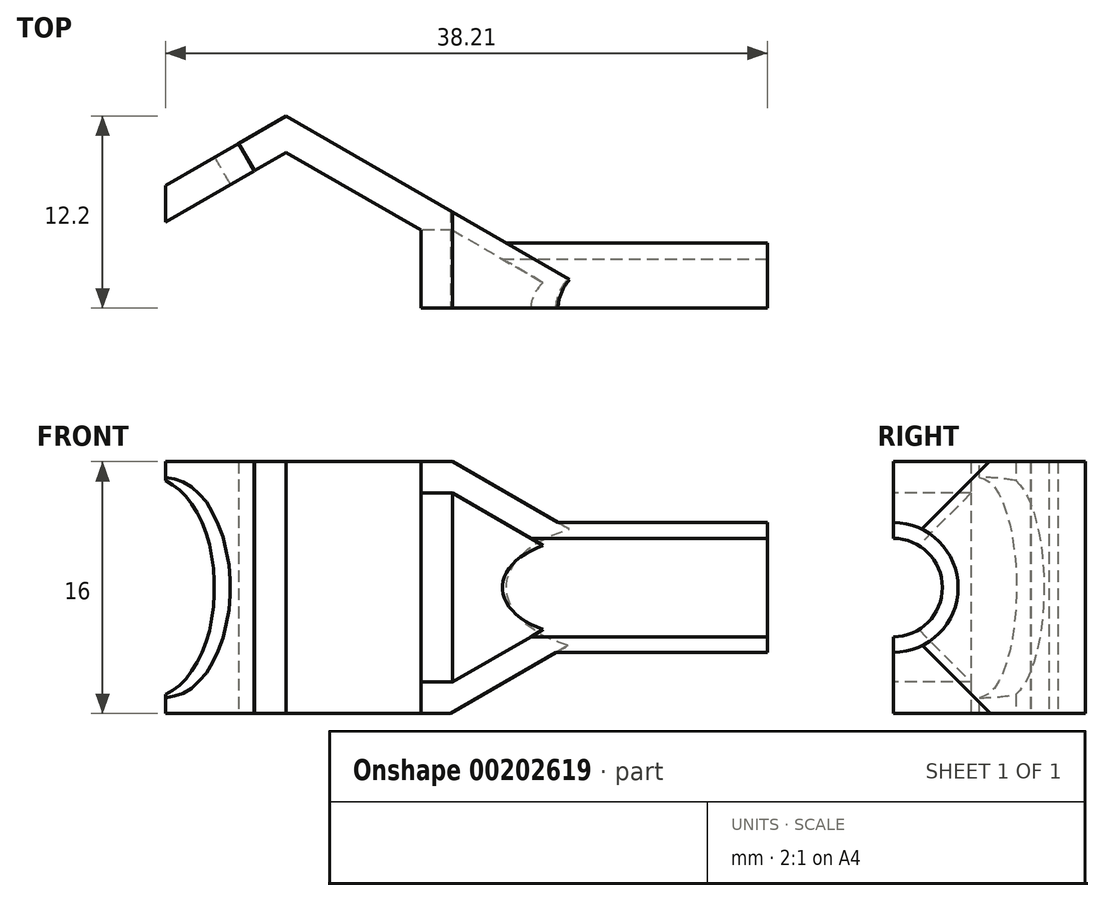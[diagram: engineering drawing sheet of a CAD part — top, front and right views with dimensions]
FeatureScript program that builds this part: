
annotation { "Feature Type Name" : "Feature", "Feature Type Description" : "" }
export const myFeature = defineFeature(function(context is Context, id is Id, definition is map)
    precondition{}
    {
        {
            var Q0;
            Q0=qCreatedBy(makeId("Top.planeOp"),FACE);
            var sketch = newSketch(context, id + "F0", { "sketchPlane" : qUnion([Q0])});
            skCircle(sketch, "E0.cCircle", {"center": v(0, 0) * mm, "radius": 9.89 * mm, "construction": true});
            skLineSegment(sketch, "E0.4", {"start": v(-2, 8.73) * mm, "end": v(0, 9.89) * mm});
            skLineSegment(sketch, "E0.5", {"start": v(0, 9.89) * mm, "end": v(8.56, 4.94) * mm});
            skLineSegment(sketch, "E1", {"start": v(0, 0) * mm, "end": v(-2, 0) * mm, "construction": true});
            skLineSegment(sketch, "E2", {"start": v(-2, 0) * mm, "end": v(-2, 14.12) * mm, "construction": true});
            skLineSegment(sketch, "E3.1", {"start": v(0, 12.2) * mm, "end": v(10.44, 6.17) * mm});
            skLineSegment(sketch, "E3.2", {"start": v(-3.02, 10.45) * mm, "end": v(0, 12.2) * mm});
            skLineSegment(sketch, "E4", {"start": v(-3.02, 10.45) * mm, "end": v(-2, 8.73) * mm});
            skPoint(sketch, "E5.orphan", {"position": v(14.51, 0) * mm});
            skPoint(sketch, "E3.0.end.orphan", {"position": v(10.5, 0) * mm});
            skLineSegment(sketch, "E6", {"start": v(8.56, 0) * mm, "end": v(10.5, 0) * mm});
            skLineSegment(sketch, "E7", {"start": v(8.56, 4.94) * mm, "end": v(8.56, 0) * mm});
            skLineSegment(sketch, "E8", {"start": v(10.44, 6.17) * mm, "end": v(21.13, 0) * mm});
            skLineSegment(sketch, "E9", {"start": v(10.5, 0) * mm, "end": v(21.13, 0) * mm});
            skSolve(sketch);
        }
        {
            var Q0;
            Q0=makeQuery(id+"F0.imprint","IMPRINT",FACE,{"disambiguationData":[TD([[makeQuery(id+"F0.imprint","IMPRINT",EDGE,{"derivedFrom":sQuery(id+"F0.wireOp",EDGE,"E0.4")}),1.0]])]});
            extrude(context, id + "F1", {"entities" : qUnion([Q0]), "depth" : 16 * mm});
        }
        {
            var Q0;
            Q0=makeQuery(id+"F1.opExtrude","SWEPT_FACE",FACE,{"disambiguationData":[OSD([sQuery(id+"F0.wireOp",EDGE,"E6"),sQuery(id+"F0.wireOp",EDGE,"E9")])]});
            var sketch = newSketch(context, id + "F2", { "sketchPlane" : qUnion([Q0])});
            skLineSegment(sketch, "E10", {"start": v(8.56, 16) * mm, "end": v(10.56, 16) * mm, "construction": true});
            skLineSegment(sketch, "E11", {"start": v(10.56, 16) * mm, "end": v(21.54, 9.66) * mm});
            skLineSegment(sketch, "E12", {"start": v(10.44, 0) * mm, "end": v(21.43, 6.35) * mm});
            skLineSegment(sketch, "E13", {"start": v(10.56, 16) * mm, "end": v(22.24, 16) * mm});
            skLineSegment(sketch, "E14", {"start": v(22.24, 16) * mm, "end": v(21.54, 9.66) * mm});
            skLineSegment(sketch, "E15", {"start": v(10.44, 0) * mm, "end": v(21.97, 0) * mm});
            skLineSegment(sketch, "E16", {"start": v(21.97, 0) * mm, "end": v(21.43, 6.35) * mm});
            skSolve(sketch);
        }
        {
            var Q0;
            {var subQ1=sQuery(id+"F2.wireOp",EDGE,"E11");var subQ2=sQuery(id+"F0.wireOp",EDGE,"E9");var subQ4=makeQuery(id+"F1.opExtrude","SWEPT_EDGE",EDGE,{"disambiguationData":[OSD([sQuery(id+"F0.wireOp",EDGE,"E8"),subQ2])]});var subQ5=makeQuery(id+"F2.imprint","INTERSECT",VERTEX,{"derivedFrom":[subQ4,subQ1]});Q0=makeQuery(id+"F2.imprint","IMPRINT",FACE,{"disambiguationData":[TD([[makeQuery(id+"F2.imprint","IMPRINT",EDGE,{"disambiguationData":[TD([[subQ5,1.0]])],"derivedFrom":subQ1}),1.0]])]});}
            var Q1;
            {var subQ1=sQuery(id+"F2.wireOp",EDGE,"E12");var subQ2=sQuery(id+"F0.wireOp",EDGE,"E9");var subQ4=makeQuery(id+"F1.opExtrude","SWEPT_EDGE",EDGE,{"disambiguationData":[OSD([sQuery(id+"F0.wireOp",EDGE,"E8"),subQ2])]});var subQ5=makeQuery(id+"F2.imprint","INTERSECT",VERTEX,{"derivedFrom":[subQ4,subQ1]});Q1=makeQuery(id+"F2.imprint","IMPRINT",FACE,{"disambiguationData":[TD([[makeQuery(id+"F2.imprint","IMPRINT",EDGE,{"disambiguationData":[TD([[subQ5,1.0]])],"derivedFrom":subQ1}),-1.0]])]});}
            extrude(context, id + "F3", {"entities" : qUnion([Q0, Q1]), "operationType" : NewBodyOperationType.REMOVE, "endBound" : BoundingType.THROUGH_ALL, "oppositeDirection" : true, "depth" : 25 * mm});
        }
        {
            var Q0;
            Q0=makeQuery(id+"F1.opExtrude","SWEPT_FACE",FACE,{"disambiguationData":[OSD([sQuery(id+"F0.wireOp",EDGE,"E7")])]});
            var sketch = newSketch(context, id + "F4", { "sketchPlane" : qUnion([Q0])});
            skArc(sketch, "E17", {"start": v(0, 12.12) * mm, "mid": v(-4.13, 8) * mm, "end": v(0, 3.88) * mm});
            skLineSegment(sketch, "E18", {"start": v(0, 0) * mm, "end": v(0, 16) * mm, "construction": true});
            skSolve(sketch);
        }
        {
            var Q0;
            {var subQ0=sQuery(id+"F4.wireOp",EDGE,"E17");Q0=makeQuery(id+"F4.imprint","IMPRINT",FACE,{"disambiguationData":[TD([[makeQuery(id+"F4.imprint","IMPRINT",EDGE,{"derivedFrom":subQ0}),1.0]])]});}
            extrude(context, id + "F5", {"entities" : qUnion([Q0]), "operationType" : NewBodyOperationType.ADD, "oppositeDirection" : true, "depth" : 22 * mm});
        }
        {
            var Q0;
            Q0=makeQuery(id+"F5.opExtrude","CAP_FACE",FACE,{"disambiguationData":[OSD([sQuery(id+"F0.wireOp",EDGE,"E6"),sQuery(id+"F0.wireOp",EDGE,"E7"),sQuery(id+"F4.wireOp",EDGE,"E17")])],"isStart":false});
            var sketch = newSketch(context, id + "F6", { "sketchPlane" : qUnion([Q0])});
            skCircle(sketch, "E19", {"center": v(0, 8) * mm, "radius": 3.12 * mm});
            skSolve(sketch);
        }
        {
            var Q0;
            {var subQ0=sQuery(id+"F6.wireOp",EDGE,"E19");var subQ1=makeQuery(id+"F5.opExtrude","CAP_EDGE",EDGE,{"disambiguationData":[OSD([sQuery(id+"F0.wireOp",EDGE,"E6"),sQuery(id+"F0.wireOp",EDGE,"E7")])],"isStart":false});var subQ2=makeQuery(id+"F6.imprint","INTERSECT",VERTEX,{"disambiguationData":[OD(0.0)],"derivedFrom":[subQ1,subQ0]});Q0=makeQuery(id+"F6.imprint","IMPRINT",FACE,{"disambiguationData":[TD([[makeQuery(id+"F6.imprint","IMPRINT",EDGE,{"disambiguationData":[TD([[subQ2,1.0]])],"derivedFrom":subQ0}),1.0]])]});}
            extrude(context, id + "F7", {"entities" : qUnion([Q0]), "operationType" : NewBodyOperationType.REMOVE, "endBound" : BoundingType.THROUGH_ALL, "oppositeDirection" : true, "depth" : 25 * mm});
        }
        {
            var Q0;
            Q0=makeQuery(id+"F1.opExtrude","SWEPT_FACE",FACE,{"disambiguationData":[OSD([sQuery(id+"F0.wireOp",EDGE,"E7")])]});
            var sketch = newSketch(context, id + "F8", { "sketchPlane" : qUnion([Q0])});
            skLineSegment(sketch, "E20", {"start": v(-4.94, 0) * mm, "end": v(-4.94, 2) * mm, "construction": true});
            skLineSegment(sketch, "E21.bottom", {"start": v(-4.94, 2) * mm, "end": v(7.06, 2) * mm});
            skLineSegment(sketch, "E21.top", {"start": v(-4.94, 14) * mm, "end": v(7.06, 14) * mm});
            skLineSegment(sketch, "E21.left", {"start": v(-4.94, 2) * mm, "end": v(-4.94, 14) * mm});
            skLineSegment(sketch, "E21.right", {"start": v(7.06, 2) * mm, "end": v(7.06, 14) * mm});
            skSolve(sketch);
        }
        {
            var Q0;
            Q0=makeQuery(id+"F1.opExtrude","SWEPT_FACE",FACE,{"disambiguationData":[OSD([sQuery(id+"F0.wireOp",EDGE,"E3.2")])]});
            var sketch = newSketch(context, id + "F9", { "sketchPlane" : qUnion([Q0])});
            skLineSegment(sketch, "E22.bottom", {"start": v(-2.6, 0) * mm, "end": v(3.9, 0) * mm});
            skLineSegment(sketch, "E22.top", {"start": v(-2.6, 16) * mm, "end": v(3.9, 16) * mm});
            skLineSegment(sketch, "E22.left", {"start": v(-2.6, 0) * mm, "end": v(-2.6, 16) * mm});
            skLineSegment(sketch, "E22.right", {"start": v(3.9, 0) * mm, "end": v(3.9, 1) * mm});
            skEllipticalArc(sketch, "E23", {});
            skLineSegment(sketch, "E24.trimOffspring", {"start": v(3.9, 15) * mm, "end": v(3.9, 16) * mm});
            const initialGuessF9  = {"E23": [0.0038915005736831387, 0.008, 0, 1, 0.007, 0.00475, 0, 3.141592653589793]};
            skSetInitialGuess(sketch, initialGuessF9);
            skSolve(sketch);
        }
        {
            var Q0;
            Q0=makeQuery(id+"F9.imprint","IMPRINT",FACE,{"disambiguationData":[TD([[makeQuery(id+"F9.imprint","IMPRINT",EDGE,{"derivedFrom":sQuery(id+"F9.wireOp",EDGE,"E22.bottom")}),1.0]])]});
            extrude(context, id + "F10", {"entities" : qUnion([Q0]), "operationType" : NewBodyOperationType.ADD, "oppositeDirection" : true, "depth" : 2 * mm});
        }
        {
            var Q0;
            Q0=makeQuery(id+"F10.opExtrude","SWEPT_FACE",FACE,{"disambiguationData":[OSD([sQuery(id+"F9.wireOp",EDGE,"E22.bottom")])]});
            var sketch = newSketch(context, id + "F11", { "sketchPlane" : qUnion([Q0])});
            skLineSegment(sketch, "E25", {"start": v(-7.65, -5.47) * mm, "end": v(-7.65, -7.78) * mm});
            skLineSegment(sketch, "E26", {"start": v(-7.65, -7.78) * mm, "end": v(-8.65, -7.2) * mm});
            skLineSegment(sketch, "E27", {"start": v(-8.65, -7.2) * mm, "end": v(-7.65, -5.47) * mm});
            skSolve(sketch);
        }
        {
            var Q0;
            Q0=makeQuery(id+"F11.imprint","IMPRINT",FACE,{"disambiguationData":[TD([[makeQuery(id+"F11.imprint","IMPRINT",EDGE,{"derivedFrom":sQuery(id+"F11.wireOp",EDGE,"E25")}),-1.0]])]});
            extrude(context, id + "F12", {"entities" : qUnion([Q0]), "operationType" : NewBodyOperationType.REMOVE, "endBound" : BoundingType.THROUGH_ALL, "oppositeDirection" : true, "depth" : 25 * mm});
        }
        {
            var Q0;
            {var subQ0=sQuery(id+"F8.wireOp",EDGE,"E21.left");Q0=makeQuery(id+"F8.imprint","IMPRINT",FACE,{"disambiguationData":[TD([[makeQuery(id+"F8.imprint","IMPRINT",EDGE,{"derivedFrom":subQ0}),1.0]])]});}
            extrude(context, id + "F13", {"entities" : qUnion([Q0]), "operationType" : NewBodyOperationType.REMOVE, "oppositeDirection" : true, "depth" : 2 * mm});
        }
        {
            var Q0;
            Q0=makeQuery(id+"F13.boolean.opBoolean","COPY",FACE,{"derivedFrom":makeQuery(id+"F13.opExtrude","CAP_FACE",FACE,{"disambiguationData":[OSD([sQuery(id+"F0.wireOp",EDGE,"E6"),sQuery(id+"F0.wireOp",EDGE,"E7"),sQuery(id+"F6.wireOp",EDGE,"E19"),sQuery(id+"F8.wireOp",EDGE,"E21.bottom"),sQuery(id+"F8.wireOp",EDGE,"E21.top"),sQuery(id+"F8.wireOp",EDGE,"E21.left")])],"isStart":false})});
            var sketch = newSketch(context, id + "F14", { "sketchPlane" : qUnion([Q0])});
            skLineSegment(sketch, "E28.bottom", {"start": v(-4.94, 2) * mm, "end": v(7.06, 2) * mm});
            skLineSegment(sketch, "E28.top", {"start": v(-4.94, 14) * mm, "end": v(7.06, 14) * mm});
            skLineSegment(sketch, "E28.left", {"start": v(-4.94, 2) * mm, "end": v(-4.94, 14) * mm});
            skLineSegment(sketch, "E28.right", {"start": v(7.06, 2) * mm, "end": v(7.06, 14) * mm});
            skSolve(sketch);
        }
        {
            var Q0;
            {var subQ2=sQuery(id+"F14.wireOp",EDGE,"E28.left");Q0=makeQuery(id+"F14.imprint","IMPRINT",FACE,{"disambiguationData":[TD([[makeQuery(id+"F14.imprint","IMPRINT",EDGE,{"derivedFrom":subQ2}),1.0]])]});}
            var Q1;
            {var subQ0=sQuery(id+"F14.wireOp",EDGE,"E28.right");Q1=makeQuery(id+"F14.imprint","IMPRINT",FACE,{"disambiguationData":[TD([[makeQuery(id+"F14.imprint","IMPRINT",EDGE,{"derivedFrom":subQ0}),1.0]])]});}
            extrude(context, id + "F15", {"entities" : qUnion([Q0, Q1]), "operationType" : NewBodyOperationType.REMOVE, "oppositeDirection" : true, "depth" : 25 * mm, "hasDraft" : true, "draftAngle" : 30 * degree, "draftPullDirection" : true});
        }
    });
